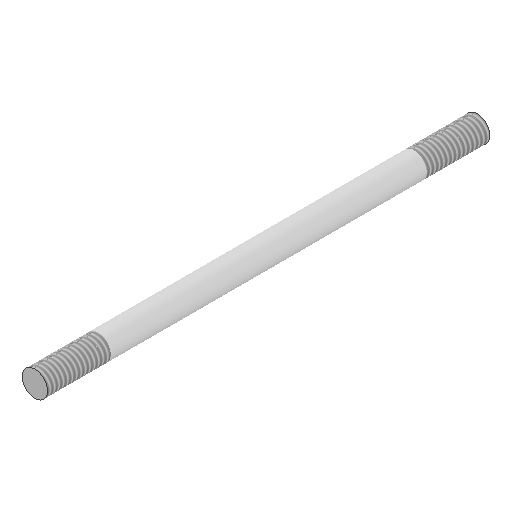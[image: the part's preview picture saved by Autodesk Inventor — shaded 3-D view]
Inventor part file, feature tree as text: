
AUTODESK INVENTOR PART (.ipt)
format: ipt  version: 2025.1 (Build 291241000, 241)  size: 102,400 bytes
history: native  units: mm
features: thread x2, other x1, extrude x1, sketch x1
ambient origin geometry x8: Origin, YZ Plane, XZ Plane, XY Plane, X Axis, Y Axis, Z Axis, Center Point
bodies: Body1 (feature_tree)
feature tree (5):
  other  "Bryła1"
  extrude  "Wyciągnięcie proste1"  Depth=4.0mm
  thread  "Gwint1"
  thread  "Gwint2"
  sketch  "Szkic1"
